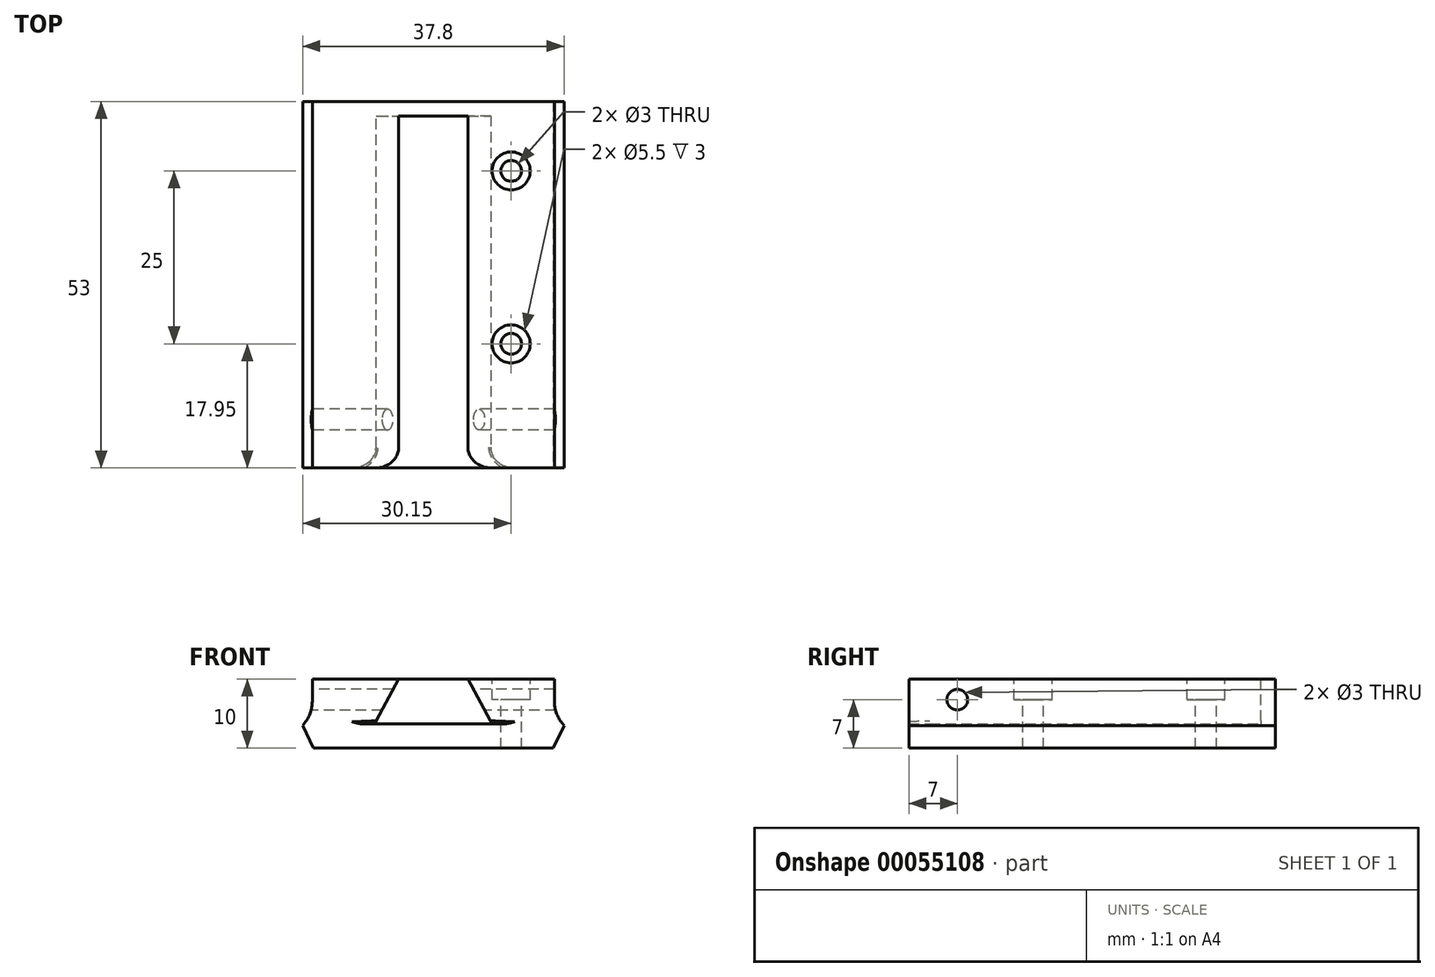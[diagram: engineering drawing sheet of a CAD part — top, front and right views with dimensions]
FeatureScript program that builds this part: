
annotation { "Feature Type Name" : "Feature", "Feature Type Description" : "" }
export const myFeature = defineFeature(function(context is Context, id is Id, definition is map)
    precondition{}
    {
        {
            var Q0;
            Q0=qCreatedBy(makeId("Front.planeOp"),FACE);
            var sketch = newSketch(context, id + "F0", { "sketchPlane" : qUnion([Q0])});
            skLineSegment(sketch, "E0.rect.top", {"start": v(17.5, 10) * mm, "end": v(5, 10) * mm});
            skLineSegment(sketch, "E0.rect.left", {"start": v(17.5, 0) * mm, "end": v(17.5, 10) * mm});
            skLineSegment(sketch, "E0.rect.right", {"start": v(-17.5, 0) * mm, "end": v(-17.5, 10) * mm});
            skPoint(sketch, "E0.rect.middle", {"position": v(0, 0) * mm});
            skLineSegment(sketch, "E1", {"start": v(-17.5, 0) * mm, "end": v(17.5, 0) * mm});
            skLineSegment(sketch, "E2", {"start": v(-8.5, 3.5) * mm, "end": v(-5, 10) * mm});
            skLineSegment(sketch, "E3.MirrorCS", {"start": v(8.5, 3.5) * mm, "end": v(5, 10) * mm});
            skLineSegment(sketch, "E4.trimOffspring", {"start": v(-5, 10) * mm, "end": v(-17.5, 10) * mm});
            skLineSegment(sketch, "E5", {"start": v(5, 10) * mm, "end": v(-5, 10) * mm});
            skLineSegment(sketch, "E6", {"start": v(-8.5, 3.5) * mm, "end": v(8.5, 3.5) * mm});
            skLineSegment(sketch, "E7", {"start": v(-17.5, 5) * mm, "end": v(-21.5, 0) * mm});
            skLineSegment(sketch, "E8", {"start": v(-21.5, 0) * mm, "end": v(-17.5, 0) * mm});
            skLineSegment(sketch, "E9", {"start": v(17.5, 0) * mm, "end": v(21.5, 0) * mm});
            skLineSegment(sketch, "E10", {"start": v(17.5, 5) * mm, "end": v(21.5, 0) * mm});
            skSolve(sketch);
        }
        {
            var Q0;
            Q0=makeQuery(id+"F0.imprint","IMPRINT",FACE,{"disambiguationData":[TD([[makeQuery(id+"F0.imprint","IMPRINT",EDGE,{"derivedFrom":sQuery(id+"F0.wireOp",EDGE,"E0.rect.top")}),1.0]])]});
            var Q1;
            {var subQ2=sQuery(id+"F0.wireOp",EDGE,"E7");Q1=makeQuery(id+"F0.imprint","IMPRINT",FACE,{"disambiguationData":[TD([[makeQuery(id+"F0.imprint","IMPRINT",EDGE,{"derivedFrom":subQ2}),1.0]])]});}
            var Q2;
            {var subQ0=sQuery(id+"F0.wireOp",EDGE,"E9");Q2=makeQuery(id+"F0.imprint","IMPRINT",FACE,{"disambiguationData":[TD([[makeQuery(id+"F0.imprint","IMPRINT",EDGE,{"derivedFrom":subQ0}),1.0]])]});}
            extrude(context, id + "F1", {"entities" : qUnion([Q0, Q1, Q2]), "depth" : (43 - 2.1 + 10) * mm});
        }
        {
            var Q0;
            Q0=makeQuery(id+"F0.imprint","IMPRINT",FACE,{"disambiguationData":[TD([[makeQuery(id+"F0.imprint","IMPRINT",EDGE,{"derivedFrom":sQuery(id+"F0.wireOp",EDGE,"E2")}),-1.0]])]});
            var Q1;
            {var subQ4=sQuery(id+"F0.wireOp",EDGE,"E0.rect.top");Q1=makeQuery(id+"F0.imprint","IMPRINT",FACE,{"disambiguationData":[TD([[makeQuery(id+"F0.imprint","IMPRINT",EDGE,{"derivedFrom":subQ4}),1.0]])]});}
            var Q2;
            {var subQ2=sQuery(id+"F0.wireOp",EDGE,"E7");Q2=makeQuery(id+"F0.imprint","IMPRINT",FACE,{"disambiguationData":[TD([[makeQuery(id+"F0.imprint","IMPRINT",EDGE,{"derivedFrom":subQ2}),1.0]])]});}
            var Q3;
            {var subQ0=sQuery(id+"F0.wireOp",EDGE,"E9");Q3=makeQuery(id+"F0.imprint","IMPRINT",FACE,{"disambiguationData":[TD([[makeQuery(id+"F0.imprint","IMPRINT",EDGE,{"derivedFrom":subQ0}),1.0]])]});}
            extrude(context, id + "F2", {"entities" : qUnion([Q0, Q1, Q2, Q3]), "operationType" : NewBodyOperationType.ADD, "oppositeDirection" : true, "depth" : 2.1 * mm});
        }
        {
            var Q0;
            {var subQ0=sQuery(id+"F0.wireOp",EDGE,"E4.trimOffspring");var subQ1=sQuery(id+"F0.wireOp",EDGE,"E0.rect.top");Q0=makeQuery(id+"F2.boolean.opBoolean","MERGE",FACE,{"derivedFrom":[makeQuery(id+"F1.opExtrude","SWEPT_FACE",FACE,{"disambiguationData":[OSD([subQ1])]}),makeQuery(id+"F1.opExtrude","SWEPT_FACE",FACE,{"disambiguationData":[OSD([subQ0])]}),makeQuery(id+"F2.opExtrude","SWEPT_FACE",FACE,{"disambiguationData":[OSD([subQ1,subQ0,sQuery(id+"F0.wireOp",EDGE,"E5")])]})]});}
            cPlane(context, id + "F3", {"entities" : qUnion([Q0]), "cplaneType" : CPlaneType.OFFSET, "offset" : 0 * mm, "width" : 150 * mm, "height" : 150 * mm});
        }
        {
            var Q0;
            {var subQ0=sQuery(id+"F0.wireOp",EDGE,"E4.trimOffspring");var subQ1=sQuery(id+"F0.wireOp",EDGE,"E0.rect.top");Q0=makeQuery(id+"F2.boolean.opBoolean","MERGE",FACE,{"derivedFrom":[makeQuery(id+"F1.opExtrude","SWEPT_FACE",FACE,{"disambiguationData":[OSD([subQ1])]}),makeQuery(id+"F1.opExtrude","SWEPT_FACE",FACE,{"disambiguationData":[OSD([subQ0])]}),makeQuery(id+"F2.opExtrude","SWEPT_FACE",FACE,{"disambiguationData":[OSD([subQ1,subQ0,sQuery(id+"F0.wireOp",EDGE,"E5")])]})]});}
            cPlane(context, id + "F4", {"entities" : qUnion([Q0]), "cplaneType" : CPlaneType.OFFSET, "offset" : 0 * mm, "width" : 150 * mm, "height" : 150 * mm});
        }
        {
            var Q0;
            Q0=qCreatedBy(id+"F4.planeOp",FACE);
            var sketch = newSketch(context, id + "F5", { "sketchPlane" : qUnion([Q0])});
            skLineSegment(sketch, "E11", {"start": v(0, 0) * mm, "end": v(0, -20.45) * mm, "construction": true});
            skLineSegment(sketch, "E12", {"start": v(0, 0) * mm, "end": v(5, 0) * mm, "construction": true});
            skLineSegment(sketch, "E13", {"start": v(5, 0) * mm, "end": v(17.5, 0) * mm, "construction": true});
            skLineSegment(sketch, "E14", {"start": v(0, -20.45) * mm, "end": v(0, -32.95) * mm, "construction": true});
            skLineSegment(sketch, "E15", {"start": v(0, -32.95) * mm, "end": v(11.25, -32.95) * mm, "construction": true});
            skPoint(sketch, "E15.endSnap0", {"position": v(11.25, 0) * mm});
            skLineSegment(sketch, "E16", {"start": v(11.25, -32.95) * mm, "end": v(11.25, -7.95) * mm, "construction": true});
            skCircle(sketch, "E17", {"center": v(11.25, -7.95) * mm, "radius": 1.5 * mm});
            skCircle(sketch, "E18", {"center": v(11.25, -7.95) * mm, "radius": 2.75 * mm});
            skCircle(sketch, "E19", {"center": v(11.25, -32.95) * mm, "radius": 1.5 * mm});
            skCircle(sketch, "E20", {"center": v(11.25, -32.95) * mm, "radius": 2.75 * mm});
            skSolve(sketch);
        }
        {
            var Q0;
            Q0=makeQuery(id+"F5.imprint","IMPRINT",FACE,{"disambiguationData":[TD([[makeQuery(id+"F5.imprint","IMPRINT",EDGE,{"derivedFrom":sQuery(id+"F5.wireOp",EDGE,"E17")}),1.0]])]});
            var Q1;
            Q1=makeQuery(id+"F5.imprint","IMPRINT",FACE,{"disambiguationData":[TD([[makeQuery(id+"F5.imprint","IMPRINT",EDGE,{"derivedFrom":sQuery(id+"F5.wireOp",EDGE,"E19")}),1.0]])]});
            extrude(context, id + "F6", {"entities" : qUnion([Q0, Q1]), "operationType" : NewBodyOperationType.REMOVE, "oppositeDirection" : true, "depth" : 25 * mm});
        }
        {
            var Q0;
            Q0 = qSketchRegion(id + "F5", true);
            extrude(context, id + "F7", {"entities" : qUnion([Q0]), "operationType" : NewBodyOperationType.REMOVE, "oppositeDirection" : true, "depth" : 3 * mm});
        }
        {
            var Q0;
            Q0=makeQuery(id+"F1.opExtrude","CAP_EDGE",EDGE,{"disambiguationData":[OSD([sQuery(id+"F0.wireOp",EDGE,"E2")])],"isStart":false});
            var Q1;
            Q1=makeQuery(id+"F1.opExtrude","CAP_EDGE",EDGE,{"disambiguationData":[OSD([sQuery(id+"F0.wireOp",EDGE,"E3.MirrorCS")])],"isStart":false});
            fillet(context, id + "F8", {"entities" : qUnion([Q0, Q1]), "radius" : 3 * mm, "tangentPropagation" : true, "allowEdgeOverflow" : false});
        }
        {
            var Q0;
            Q0=qCreatedBy(makeId("Right.planeOp"),FACE);
            var sketch = newSketch(context, id + "F9", { "sketchPlane" : qUnion([Q0])});
            skLineSegment(sketch, "E21", {"start": v(0, 0) * mm, "end": v(-43.9, 0) * mm, "construction": true});
            skPoint(sketch, "E22.center.orphan", {"position": v(-43.9, 5) * mm});
            skPoint(sketch, "E23.orphan", {"position": v(-43.9, 10) * mm});
            skLineSegment(sketch, "E24", {"start": v(-43.9, 0) * mm, "end": v(-43.9, 7) * mm});
            skCircle(sketch, "E25", {"center": v(-43.9, 7) * mm, "radius": 1.5 * mm});
            skSolve(sketch);
        }
        {
            var Q0;
            Q0 = qSketchRegion(id + "F9", true);
            extrude(context, id + "F10", {"entities" : qUnion([Q0]), "operationType" : NewBodyOperationType.REMOVE, "endBound" : BoundingType.THROUGH_ALL, "depth" : 25 * mm, "hasSecondDirection" : true, "secondDirectionBound" : SecondDirectionBoundingType.THROUGH_ALL, "secondDirectionOppositeDirection" : true, "secondDirectionDepth" : 25 * mm});
        }
        {
            var Q0;
            {var subQ0=sQuery(id+"F0.wireOp",EDGE,"E3.MirrorCS");var subQ1=sQuery(id+"F0.wireOp",EDGE,"E6");Q0=makeQuery(id+"F10.boolean.opBoolean","SPLIT",EDGE,{"disambiguationData":[TD([makeQuery(id+"F2.opExtrude","CAP_FACE",FACE,{"disambiguationData":[OSD([sQuery(id+"F0.wireOp",EDGE,"E0.rect.top"),sQuery(id+"F0.wireOp",EDGE,"E0.rect.left"),sQuery(id+"F0.wireOp",EDGE,"E0.rect.right"),sQuery(id+"F0.wireOp",EDGE,"E1"),sQuery(id+"F0.wireOp",EDGE,"E4.trimOffspring"),sQuery(id+"F0.wireOp",EDGE,"E5")])],"isStart":true})])],"derivedFrom":makeQuery(id+"F1.opExtrude","SWEPT_EDGE",EDGE,{"disambiguationData":[OSD([subQ0,subQ1])]})});}
            var Q1;
            {var subQ0=sQuery(id+"F0.wireOp",EDGE,"E2");var subQ1=sQuery(id+"F0.wireOp",EDGE,"E6");Q1=makeQuery(id+"F10.boolean.opBoolean","SPLIT",EDGE,{"disambiguationData":[TD([makeQuery(id+"F2.opExtrude","CAP_FACE",FACE,{"disambiguationData":[OSD([sQuery(id+"F0.wireOp",EDGE,"E0.rect.top"),sQuery(id+"F0.wireOp",EDGE,"E0.rect.left"),sQuery(id+"F0.wireOp",EDGE,"E0.rect.right"),sQuery(id+"F0.wireOp",EDGE,"E1"),sQuery(id+"F0.wireOp",EDGE,"E4.trimOffspring"),sQuery(id+"F0.wireOp",EDGE,"E5")])],"isStart":true})])],"derivedFrom":makeQuery(id+"F1.opExtrude","SWEPT_EDGE",EDGE,{"disambiguationData":[OSD([subQ0,subQ1])]})});}
            fillet(context, id + "F11", {"entities" : qUnion([Q0, Q1]), "radius" : 0.3 * mm, "tangentPropagation" : true, "allowEdgeOverflow" : false});
        }
        {
            var Q0;
            {var subQ0=sQuery(id+"F0.wireOp",EDGE,"E10");var subQ1=sQuery(id+"F0.wireOp",EDGE,"E0.rect.left");Q0=makeQuery(id+"F2.boolean.opBoolean","MERGE",EDGE,{"derivedFrom":[makeQuery(id+"F1.opExtrude","SWEPT_EDGE",EDGE,{"disambiguationData":[OSD([subQ1,subQ0])]}),makeQuery(id+"F2.opExtrude","SWEPT_EDGE",EDGE,{"disambiguationData":[OSD([subQ1,subQ0])]})]});}
            var Q1;
            {var subQ0=sQuery(id+"F0.wireOp",EDGE,"E7");var subQ1=sQuery(id+"F0.wireOp",EDGE,"E0.rect.right");Q1=makeQuery(id+"F2.boolean.opBoolean","MERGE",EDGE,{"derivedFrom":[makeQuery(id+"F1.opExtrude","SWEPT_EDGE",EDGE,{"disambiguationData":[OSD([subQ1,subQ0])]}),makeQuery(id+"F2.opExtrude","SWEPT_EDGE",EDGE,{"disambiguationData":[OSD([subQ1,subQ0])]})]});}
            fillet(context, id + "F12", {"entities" : qUnion([Q0, Q1]), "radius" : 5 * mm, "tangentPropagation" : true, "allowEdgeOverflow" : false});
        }
        {
            var Q0;
            {var subQ0=sQuery(id+"F0.wireOp",EDGE,"E8");var subQ1=sQuery(id+"F0.wireOp",EDGE,"E7");Q0=makeQuery(id+"F2.boolean.opBoolean","MERGE",EDGE,{"derivedFrom":[makeQuery(id+"F1.opExtrude","SWEPT_EDGE",EDGE,{"disambiguationData":[OSD([subQ1,subQ0])]}),makeQuery(id+"F2.opExtrude","SWEPT_EDGE",EDGE,{"disambiguationData":[OSD([subQ1,subQ0])]})]});}
            var Q1;
            {var subQ0=sQuery(id+"F0.wireOp",EDGE,"E10");var subQ1=sQuery(id+"F0.wireOp",EDGE,"E9");Q1=makeQuery(id+"F2.boolean.opBoolean","MERGE",EDGE,{"derivedFrom":[makeQuery(id+"F1.opExtrude","SWEPT_EDGE",EDGE,{"disambiguationData":[OSD([subQ1,subQ0])]}),makeQuery(id+"F2.opExtrude","SWEPT_EDGE",EDGE,{"disambiguationData":[OSD([subQ1,subQ0])]})]});}
            chamfer(context, id + "F13", {"entities" : qUnion([Q0, Q1]), "width" : 2 * mm, "tangentPropagation" : true});
        }
    });
